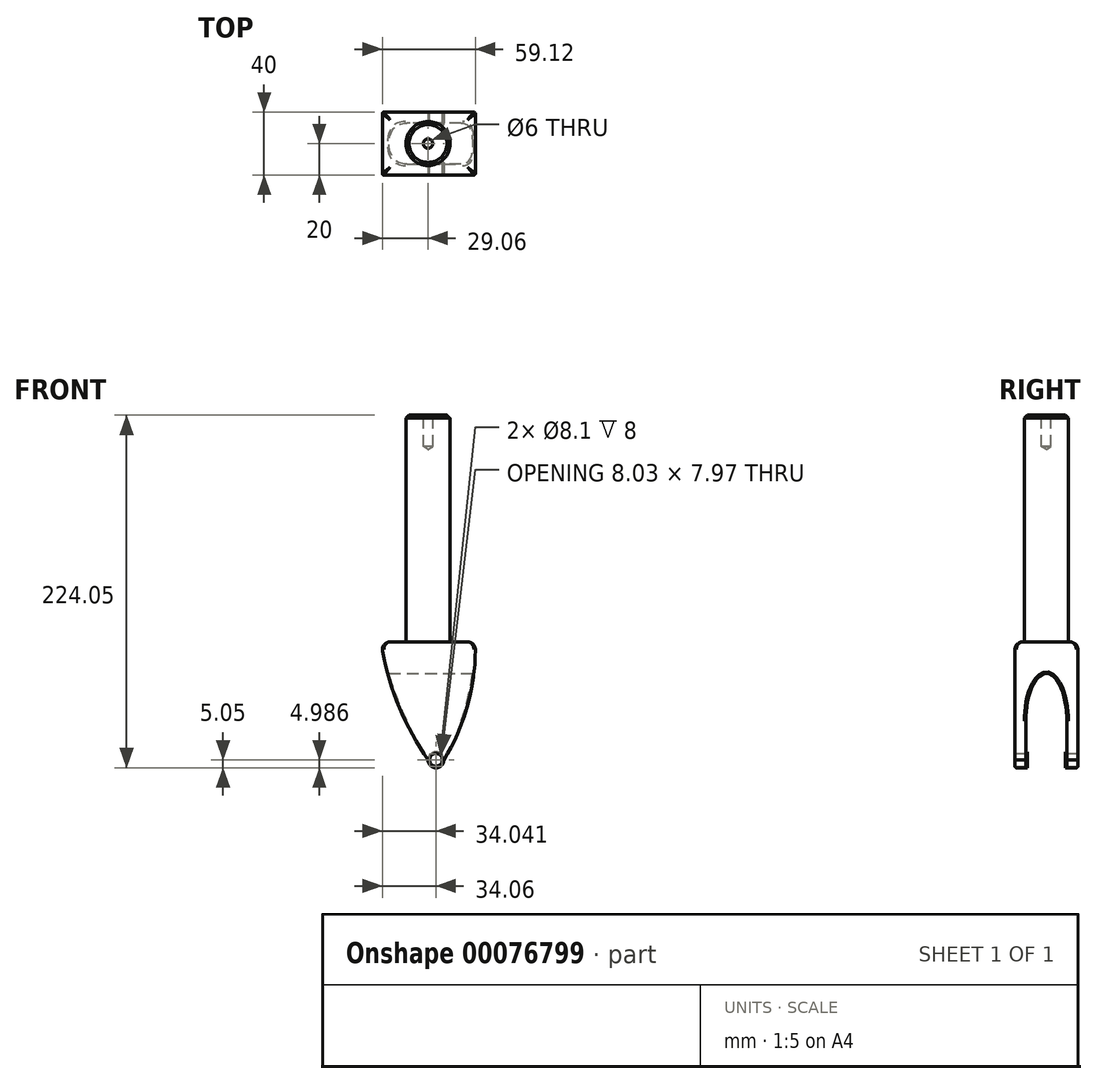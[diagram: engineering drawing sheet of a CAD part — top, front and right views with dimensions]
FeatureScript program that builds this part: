
annotation { "Feature Type Name" : "Feature", "Feature Type Description" : "" }
export const myFeature = defineFeature(function(context is Context, id is Id, definition is map)
    precondition{}
    {
        {
            var Q0;
            Q0=qCreatedBy(makeId("Top.planeOp"),FACE);
            var sketch = newSketch(context, id + "F0", { "sketchPlane" : qUnion([Q0])});
            skCircle(sketch, "E0", {"center": v(0, 0) * mm, "radius": 14 * mm});
            skSolve(sketch);
        }
        {
            var Q0;
            Q0 = qSketchRegion(id + "F0", true);
            extrude(context, id + "F1", {"entities" : qUnion([Q0]), "depth" : 144 * mm});
        }
        {
            var Q0;
            Q0=qCreatedBy(makeId("Top.planeOp"),FACE);
            var sketch = newSketch(context, id + "F2", { "sketchPlane" : qUnion([Q0])});
            skLineSegment(sketch, "E1.bottom", {"start": v(40, -20) * mm, "end": v(-40, -20) * mm});
            skLineSegment(sketch, "E1.top", {"start": v(40, 20) * mm, "end": v(-40, 20) * mm});
            skLineSegment(sketch, "E1.left", {"start": v(40, -20) * mm, "end": v(40, 20) * mm});
            skLineSegment(sketch, "E1.right", {"start": v(-40, -20) * mm, "end": v(-40, 20) * mm});
            skPoint(sketch, "E1.middle", {"position": v(0, 0) * mm});
            skSolve(sketch);
        }
        {
            var Q0;
            Q0 = qSketchRegion(id + "F2", true);
            extrude(context, id + "F3", {"entities" : qUnion([Q0]), "operationType" : NewBodyOperationType.ADD, "oppositeDirection" : true, "depth" : 80 * mm});
        }
        {
            var Q0;
            Q0=makeQuery(id+"F3.opExtrude","SWEPT_EDGE",EDGE,{"disambiguationData":[OSD([sQuery(id+"F2.wireOp",EDGE,"E1.bottom"),sQuery(id+"F2.wireOp",EDGE,"E1.left")])]});
            var Q1;
            Q1=makeQuery(id+"F3.opExtrude","SWEPT_EDGE",EDGE,{"disambiguationData":[OSD([sQuery(id+"F2.wireOp",EDGE,"E1.bottom"),sQuery(id+"F2.wireOp",EDGE,"E1.right")])]});
            var Q2;
            Q2=makeQuery(id+"F3.opExtrude","SWEPT_EDGE",EDGE,{"disambiguationData":[OSD([sQuery(id+"F2.wireOp",EDGE,"E1.top"),sQuery(id+"F2.wireOp",EDGE,"E1.right")])]});
            var Q3;
            Q3=makeQuery(id+"F3.opExtrude","SWEPT_EDGE",EDGE,{"disambiguationData":[OSD([sQuery(id+"F2.wireOp",EDGE,"E1.top"),sQuery(id+"F2.wireOp",EDGE,"E1.left")])]});
            fillet(context, id + "F4", {"entities" : qUnion([Q0, Q1, Q2, Q3]), "radius" : 5 * mm, "tangentPropagation" : true, "allowEdgeOverflow" : false});
        }
        {
            var Q0;
            Q0=qCreatedBy(makeId("Front.planeOp"),FACE);
            var sketch = newSketch(context, id + "F5", { "sketchPlane" : qUnion([Q0])});
            skPoint(sketch, "E2", {"position": v(-35.6, 0) * mm});
            skPoint(sketch, "E3", {"position": v(-30, 0) * mm});
            skLineSegment(sketch, "E4", {"start": v(-30, -90) * mm, "end": v(30, -90) * mm});
            skLineSegment(sketch, "E5", {"start": v(30, -8.37) * mm, "end": v(30, 0) * mm});
            skLineSegment(sketch, "E6", {"start": v(30, 0) * mm, "end": v(-30, 0) * mm});
            skPoint(sketch, "E7", {"position": v(5, -75) * mm});
            skArc(sketch, "E8", {"start": v(0, -75) * mm, "mid": v(5, -80) * mm, "end": v(10, -75) * mm});
            skLineSegment(sketch, "E9", {"start": v(10, -75) * mm, "end": v(0, -75) * mm});
            skArc(sketch, "E10", {"start": v(-30, 0) * mm, "mid": v(-19.26, -39.2) * mm, "end": v(0, -75) * mm});
            skArc(sketch, "E11", {"start": v(10, -75) * mm, "mid": v(25.5, -38.97) * mm, "end": v(30, 0) * mm});
            skLineSegment(sketch, "E12", {"start": v(30, 0) * mm, "end": v(43.9, 0) * mm});
            skLineSegment(sketch, "E13", {"start": v(43.9, 0) * mm, "end": v(41.1, -18.15) * mm});
            skLineSegment(sketch, "E14", {"start": v(-30, 0) * mm, "end": v(-45.43, 0) * mm});
            skLineSegment(sketch, "E15", {"start": v(-45.43, 0) * mm, "end": v(-66.81, -82.88) * mm});
            skLineSegment(sketch, "E16", {"start": v(-66.81, -82.88) * mm, "end": v(-30, -90) * mm});
            skLineSegment(sketch, "E17", {"start": v(41.1, -18.15) * mm, "end": v(46.7, -90.87) * mm});
            skLineSegment(sketch, "E18", {"start": v(46.7, -90.87) * mm, "end": v(30, -90) * mm});
            skSolve(sketch);
        }
        {
            var Q0;
            Q0=qCreatedBy(makeId("Right.planeOp"),FACE);
            var sketch = newSketch(context, id + "F6", { "sketchPlane" : qUnion([Q0])});
            skEllipticalArc(sketch, "E19", {});
            skLineSegment(sketch, "E20", {"start": v(13, -50) * mm, "end": v(13, -80) * mm});
            skLineSegment(sketch, "E21", {"start": v(13, -80) * mm, "end": v(-13, -80) * mm});
            skPoint(sketch, "E21.endSnap0", {"position": v(-13, -50) * mm});
            skLineSegment(sketch, "E22", {"start": v(-13, -80) * mm, "end": v(-13, -50) * mm});
            skPoint(sketch, "E23", {"position": v(0, -20) * mm});
            const initialGuessF6  = {"E19": [0, -0.05, 0, 1, 0.03, 0.013, 4.71238898038469, 1.5707963267948966]};
            skSetInitialGuess(sketch, initialGuessF6);
            skSolve(sketch);
        }
        {
            var Q0;
            Q0=makeQuery(id+"F5.imprint","IMPRINT",FACE,{"disambiguationData":[TD([[makeQuery(id+"F5.imprint","IMPRINT",EDGE,{"derivedFrom":sQuery(id+"F5.wireOp",EDGE,"E4")}),1.0]])]});
            extrude(context, id + "F7", {"entities" : qUnion([Q0]), "operationType" : NewBodyOperationType.REMOVE, "oppositeDirection" : true, "depth" : 4444 * mm, "hasSecondDirection" : true, "secondDirectionOppositeDirection" : false, "secondDirectionDepth" : 25 * mm});
        }
        {
            var Q0;
            Q0 = qSketchRegion(id + "F6", true);
            extrude(context, id + "F8", {"entities" : qUnion([Q0]), "operationType" : NewBodyOperationType.REMOVE, "endBound" : BoundingType.SYMMETRIC, "depth" : 70 * mm});
        }
        {
            var Q0;
            Q0=makeQuery(id+"F3.opExtrude","SWEPT_FACE",FACE,{"disambiguationData":[OSD([sQuery(id+"F2.wireOp",EDGE,"E1.top")])]});
            var sketch = newSketch(context, id + "F9", { "sketchPlane" : qUnion([Q0])});
            skPoint(sketch, "E24", {"position": v(-5, -75) * mm});
            skSolve(sketch);
        }
        {
            var Q0;
            Q0=sQuery(id+"F9.wireOp",VERTEX,"E24");
            var Q1;
            Q1=makeQuery(id+"F1.opExtrude","SWEPT_BODY",BODY,{"disambiguationData":[OSD([sQuery(id+"F0.wireOp",EDGE,"E0")])]});
            hole(context, id + "F10", {"style" : HoleStyle.SIMPLE, "endStyle" : HoleEndStyle.THROUGH, "holeDiameter" : 8.1 * mm, "locations" : qUnion([Q0]), "scope" : qUnion([Q1]), "isTappedThrough" : true});
        }
        {
            var Q0;
            Q0=makeQuery(id+"F8.boolean.opBoolean","COPY",FACE,{"derivedFrom":makeQuery(id+"F8.opExtrude","SWEPT_FACE",FACE,{"disambiguationData":[OSD([sQuery(id+"F6.wireOp",EDGE,"E22")])]})});
            var sketch = newSketch(context, id + "F11", { "sketchPlane" : qUnion([Q0])});
            skCircle(sketch, "E25.0", {"center": v(-5, -75) * mm, "radius": 4.05 * mm});
            skCircle(sketch, "E26.0", {"center": v(-5, -75) * mm, "radius": 5.05 * mm});
            skSolve(sketch);
        }
        {
            var Q0;
            Q0 = qSketchRegion(id + "F11", true);
            extrude(context, id + "F12", {"entities" : qUnion([Q0]), "depth" : 1 * mm});
        }
        {
            var Q0;
            Q0=makeQuery(id+"F12.opExtrude","SWEPT_BODY",BODY,{"disambiguationData":[OSD([sQuery(id+"F11.wireOp",EDGE,"E25.0"),sQuery(id+"F11.wireOp",EDGE,"E26.0")])]});
            var Q1;
            Q1=qCreatedBy(makeId("Front.planeOp"),FACE);
            mirror(context, id + "F13", {"operationType" : NewBodyOperationType.ADD, "entities" : qUnion([Q0]), "mirrorPlane" : qUnion([Q1])});
        }
        {
            var Q0;
            Q0=makeQuery(id+"F1.opExtrude","CAP_FACE",FACE,{"disambiguationData":[OSD([sQuery(id+"F0.wireOp",EDGE,"E0")])],"isStart":false});
            var sketch = newSketch(context, id + "F14", { "sketchPlane" : qUnion([Q0])});
            skPoint(sketch, "E27", {"position": v(0, 0) * mm});
            skSolve(sketch);
        }
        {
            var Q0;
            Q0=sQuery(id+"F14.wireOp",VERTEX,"E27");
            var Q1;
            Q1=makeQuery(id+"F1.opExtrude","SWEPT_BODY",BODY,{"disambiguationData":[OSD([sQuery(id+"F0.wireOp",EDGE,"E0")])]});
            hole(context, id + "F15", {"style" : HoleStyle.SIMPLE, "endStyle" : HoleEndStyle.BLIND, "holeDiameter" : 6 * mm, "holeDepth" : 20 * mm, "locations" : qUnion([Q0]), "scope" : qUnion([Q1])});
        }
        {
            var Q0;
            Q0=makeQuery(id+"F1.opExtrude","CAP_EDGE",EDGE,{"disambiguationData":[OSD([sQuery(id+"F0.wireOp",EDGE,"E0")])],"isStart":false});
            chamfer(context, id + "F16", {"entities" : qUnion([Q0]), "width" : 2 * mm, "tangentPropagation" : true});
        }
        {
            var Q0;
            Q0=makeQuery(id+"F8.boolean.opBoolean","INTERSECT",EDGE,{"derivedFrom":[makeQuery(id+"F7.boolean.opBoolean","COPY",FACE,{"derivedFrom":makeQuery(id+"F7.opExtrude","SWEPT_FACE",FACE,{"disambiguationData":[OSD([sQuery(id+"F5.wireOp",EDGE,"E11")])]})}),makeQuery(id+"F8.opExtrude","SWEPT_FACE",FACE,{"disambiguationData":[OSD([sQuery(id+"F6.wireOp",EDGE,"E19")])]})]});
            var Q1;
            {var subQ1=makeQuery(id+"F8.opExtrude","SWEPT_FACE",FACE,{"disambiguationData":[OSD([sQuery(id+"F6.wireOp",EDGE,"E22")])]});var subQ2=makeQuery(id+"F7.boolean.opBoolean","COPY",FACE,{"derivedFrom":makeQuery(id+"F7.opExtrude","SWEPT_FACE",FACE,{"disambiguationData":[OSD([sQuery(id+"F5.wireOp",EDGE,"E11")])]})});Q1=makeQuery(id+"F13.boolean.opBoolean","SPLIT",EDGE,{"disambiguationData":[TD([makeQuery(id+"F8.boolean.opBoolean","COPY",FACE,{"derivedFrom":makeQuery(id+"F8.opExtrude","SWEPT_FACE",FACE,{"disambiguationData":[OSD([sQuery(id+"F6.wireOp",EDGE,"E19")])]})})])],"derivedFrom":makeQuery(id+"F8.boolean.opBoolean","INTERSECT",EDGE,{"derivedFrom":[subQ2,subQ1]})});}
            var Q2;
            Q2=makeQuery(id+"F7.boolean.opBoolean","INTERSECT",EDGE,{"derivedFrom":[makeQuery(id+"F3.opExtrude","SWEPT_FACE",FACE,{"disambiguationData":[OSD([sQuery(id+"F2.wireOp",EDGE,"E1.bottom")])]}),makeQuery(id+"F7.opExtrude","SWEPT_FACE",FACE,{"disambiguationData":[OSD([sQuery(id+"F5.wireOp",EDGE,"E11")])]})]});
            var Q3;
            Q3=makeQuery(id+"F7.boolean.opBoolean","INTERSECT",EDGE,{"derivedFrom":[makeQuery(id+"F3.opExtrude","SWEPT_FACE",FACE,{"disambiguationData":[OSD([sQuery(id+"F2.wireOp",EDGE,"E1.top")])]}),makeQuery(id+"F7.opExtrude","SWEPT_FACE",FACE,{"disambiguationData":[OSD([sQuery(id+"F5.wireOp",EDGE,"E11")])]})]});
            var Q4;
            {var subQ1=makeQuery(id+"F8.opExtrude","SWEPT_FACE",FACE,{"disambiguationData":[OSD([sQuery(id+"F6.wireOp",EDGE,"E20")])]});var subQ2=makeQuery(id+"F7.boolean.opBoolean","COPY",FACE,{"derivedFrom":makeQuery(id+"F7.opExtrude","SWEPT_FACE",FACE,{"disambiguationData":[OSD([sQuery(id+"F5.wireOp",EDGE,"E11")])]})});Q4=makeQuery(id+"F13.boolean.opBoolean","SPLIT",EDGE,{"disambiguationData":[TD([makeQuery(id+"F8.boolean.opBoolean","COPY",FACE,{"derivedFrom":makeQuery(id+"F8.opExtrude","SWEPT_FACE",FACE,{"disambiguationData":[OSD([sQuery(id+"F6.wireOp",EDGE,"E19")])]})})])],"derivedFrom":makeQuery(id+"F8.boolean.opBoolean","INTERSECT",EDGE,{"derivedFrom":[subQ2,subQ1]})});}
            var Q5;
            Q5=makeQuery(id+"F7.boolean.opBoolean","INTERSECT",EDGE,{"derivedFrom":[makeQuery(id+"F3.opExtrude","SWEPT_FACE",FACE,{"disambiguationData":[OSD([sQuery(id+"F2.wireOp",EDGE,"E1.bottom")])]}),makeQuery(id+"F7.opExtrude","SWEPT_FACE",FACE,{"disambiguationData":[OSD([sQuery(id+"F5.wireOp",EDGE,"E10")])]})]});
            var Q6;
            Q6=makeQuery(id+"F7.boolean.opBoolean","INTERSECT",EDGE,{"derivedFrom":[makeQuery(id+"F3.opExtrude","SWEPT_FACE",FACE,{"disambiguationData":[OSD([sQuery(id+"F2.wireOp",EDGE,"E1.bottom")])]}),makeQuery(id+"F7.opExtrude","SWEPT_FACE",FACE,{"disambiguationData":[OSD([sQuery(id+"F5.wireOp",EDGE,"E8")])]})]});
            var Q7;
            Q7=makeQuery(id+"F7.boolean.opBoolean","INTERSECT",EDGE,{"derivedFrom":[makeQuery(id+"F3.opExtrude","SWEPT_FACE",FACE,{"disambiguationData":[OSD([sQuery(id+"F2.wireOp",EDGE,"E1.top")])]}),makeQuery(id+"F7.opExtrude","SWEPT_FACE",FACE,{"disambiguationData":[OSD([sQuery(id+"F5.wireOp",EDGE,"E8")])]})]});
            var Q8;
            Q8=makeQuery(id+"F7.boolean.opBoolean","INTERSECT",EDGE,{"derivedFrom":[makeQuery(id+"F3.opExtrude","SWEPT_FACE",FACE,{"disambiguationData":[OSD([sQuery(id+"F2.wireOp",EDGE,"E1.top")])]}),makeQuery(id+"F7.opExtrude","SWEPT_FACE",FACE,{"disambiguationData":[OSD([sQuery(id+"F5.wireOp",EDGE,"E10")])]})]});
            var Q9;
            Q9=makeQuery(id+"F8.boolean.opBoolean","INTERSECT",EDGE,{"derivedFrom":[makeQuery(id+"F7.boolean.opBoolean","COPY",FACE,{"derivedFrom":makeQuery(id+"F7.opExtrude","SWEPT_FACE",FACE,{"disambiguationData":[OSD([sQuery(id+"F5.wireOp",EDGE,"E10")])]})}),makeQuery(id+"F8.opExtrude","SWEPT_FACE",FACE,{"disambiguationData":[OSD([sQuery(id+"F6.wireOp",EDGE,"E19")])]})]});
            var Q10;
            {var subQ1=makeQuery(id+"F8.opExtrude","SWEPT_FACE",FACE,{"disambiguationData":[OSD([sQuery(id+"F6.wireOp",EDGE,"E20")])]});var subQ2=makeQuery(id+"F7.boolean.opBoolean","COPY",FACE,{"derivedFrom":makeQuery(id+"F7.opExtrude","SWEPT_FACE",FACE,{"disambiguationData":[OSD([sQuery(id+"F5.wireOp",EDGE,"E10")])]})});Q10=makeQuery(id+"F13.boolean.opBoolean","SPLIT",EDGE,{"disambiguationData":[TD([makeQuery(id+"F8.boolean.opBoolean","COPY",FACE,{"derivedFrom":makeQuery(id+"F8.opExtrude","SWEPT_FACE",FACE,{"disambiguationData":[OSD([sQuery(id+"F6.wireOp",EDGE,"E19")])]})})])],"derivedFrom":makeQuery(id+"F8.boolean.opBoolean","INTERSECT",EDGE,{"derivedFrom":[subQ2,subQ1]})});}
            var Q11;
            {var subQ1=makeQuery(id+"F8.opExtrude","SWEPT_FACE",FACE,{"disambiguationData":[OSD([sQuery(id+"F6.wireOp",EDGE,"E22")])]});var subQ2=makeQuery(id+"F7.boolean.opBoolean","COPY",FACE,{"derivedFrom":makeQuery(id+"F7.opExtrude","SWEPT_FACE",FACE,{"disambiguationData":[OSD([sQuery(id+"F5.wireOp",EDGE,"E10")])]})});Q11=makeQuery(id+"F13.boolean.opBoolean","SPLIT",EDGE,{"disambiguationData":[TD([makeQuery(id+"F8.boolean.opBoolean","COPY",FACE,{"derivedFrom":makeQuery(id+"F8.opExtrude","SWEPT_FACE",FACE,{"disambiguationData":[OSD([sQuery(id+"F6.wireOp",EDGE,"E19")])]})})])],"derivedFrom":makeQuery(id+"F8.boolean.opBoolean","INTERSECT",EDGE,{"derivedFrom":[subQ2,subQ1]})});}
            fillet(context, id + "F17", {"entities" : qUnion([Q0, Q1, Q2, Q3, Q4, Q5, Q6, Q7, Q8, Q9, Q10, Q11]), "radius" : 1 * mm, "tangentPropagation" : true, "allowEdgeOverflow" : false});
        }
        {
            var Q0;
            Q0=makeQuery(id+"F3.opExtrude","CAP_EDGE",EDGE,{"disambiguationData":[OSD([sQuery(id+"F2.wireOp",EDGE,"E1.bottom")])],"isStart":true});
            var Q1;
            Q1=makeQuery(id+"F7.boolean.opBoolean","COPY",EDGE,{"derivedFrom":makeQuery(id+"F7.opExtrude","SWEPT_EDGE",EDGE,{"disambiguationData":[OSD([sQuery(id+"F5.wireOp",EDGE,"E5"),sQuery(id+"F5.wireOp",EDGE,"E6"),sQuery(id+"F5.wireOp",EDGE,"E11"),sQuery(id+"F5.wireOp",EDGE,"E12")])]})});
            var Q2;
            Q2=makeQuery(id+"F3.opExtrude","CAP_EDGE",EDGE,{"disambiguationData":[OSD([sQuery(id+"F2.wireOp",EDGE,"E1.top")])],"isStart":true});
            var Q3;
            Q3=makeQuery(id+"F7.boolean.opBoolean","COPY",EDGE,{"derivedFrom":makeQuery(id+"F7.opExtrude","SWEPT_EDGE",EDGE,{"disambiguationData":[OSD([sQuery(id+"F5.wireOp",EDGE,"E6"),sQuery(id+"F5.wireOp",EDGE,"E10"),sQuery(id+"F5.wireOp",EDGE,"E14")])]})});
            fillet(context, id + "F18", {"entities" : qUnion([Q0, Q1, Q2, Q3]), "radius" : 5 * mm, "tangentPropagation" : true, "allowEdgeOverflow" : false});
        }
    });
